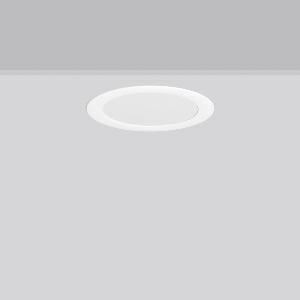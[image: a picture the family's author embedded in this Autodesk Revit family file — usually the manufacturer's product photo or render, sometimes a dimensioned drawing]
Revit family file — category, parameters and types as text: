
# Revit family: toledo_flat_round_e_672224_002_1_04_5b04
name_source: partatom
category: Lighting Fixtures
units: mm (PartAtom-declared; Revit-internal decimal feet)

## family parameters
Cut with Voids When Loaded = No
Host = Face
Light Source = No
Part Type = Normal
Room Calculation Point = No
Round Connector Dimension = Use Diameter
Shared = No

## types (1)
- TOLEDO FLAT round E (1 x LED Modul 840, 1800 lm, 4000)
    Apparent Load = 17 VA
    CIE Flux Codes = 48 79 96 100 100
    Color Rendering = 80
    Color Temperature = 4000
    Default Elevation = 1800 mm
    Description = Series: TOLEDO FLAT round
Ultra thin recessed downlight. For escape route illumination. Housing: die-cast aluminium, powder-coated. Lightguide and diffuser made of non-yellowing plastic (PMMA). Diffuser opal matt plastic. Ceiling installation with spring system. Including separate LED converter with connecting cable 250 mm. Self-contained system with automatic self-test and feedback to the RZB monitoring system MULTIDIGIT. External driver with simple plug-in locking system. 
Colour: white
Diameter: 255 mm
Height: 3 mm
Cut-out diameter: 234 mm
Recess height: 100 mm
Luminaire: recess height: 60-80 mm
Weight: 1.77 kg
Operating mode: maintained power mode
Duration time: 3 h
Lamp: LED
Socket: without socket
Colour temperature: 4000K
Colour rendering index (CRI): 80
System power: 17 W
Rated luminous flux: 1800 lm
Luminous flux, emergency: 460 lm
System power, emergency: -
Control gear: Regulated power supply
Protection class: I
Type of protection: IP 54
    Height = 0 mm  [stored 0 ft]
    Lamp = 1 x LED Modul 840
    Lamp Light Flux = 1800 lm
    Lamp count = 1
    Length = 255 mm
    Lifetime = 50000 h
    Luminous efficacy = 106 lm/W
    Manufacturer = RZB
    ModVariant = No
    Model = 672224.002.1.04
    Mounting Place = Ceiling
    Mounting Type = Recessed
    Number of Poles = 1
    OnlyDefault = Yes
    Power Factor = 1
    Product Name = TOLEDO FLAT round E
    Product group = Recessed downlights
    ProductGroupID = 402
    Protection Class = Protection class I
    Protection Degree = IP 40
    RLX_Detail_Level = 1
    RLX_Emergency_Light_Flux = 460 lm
    RLX_Emergency_Type = 3
    RLX_Emergency_Type_DB = Yes
    RlxData = <blob elided: 30605 chars, md5=63955d29>
    Socket = socket
    Standby Power = 0 W
    System Light Flux = 1800 lm
    System Power = 17 W
    Type Comments = Product without accessories
    Type Image = 901453.002.jpg
    URL = http://relux.com
    VarID = ---
    Voltage = 0 V
    Weight = 0.00 kg
    Width = 0 mm  [stored 0 ft]

note: [stored X ft] marks values corroborated as IEEE doubles in the binary element streams (Revit-internal decimal feet)

## geometry (parser evidence)
native form markers: Blend x4, Sweep x10
no freeform markers — native parametric forms only
